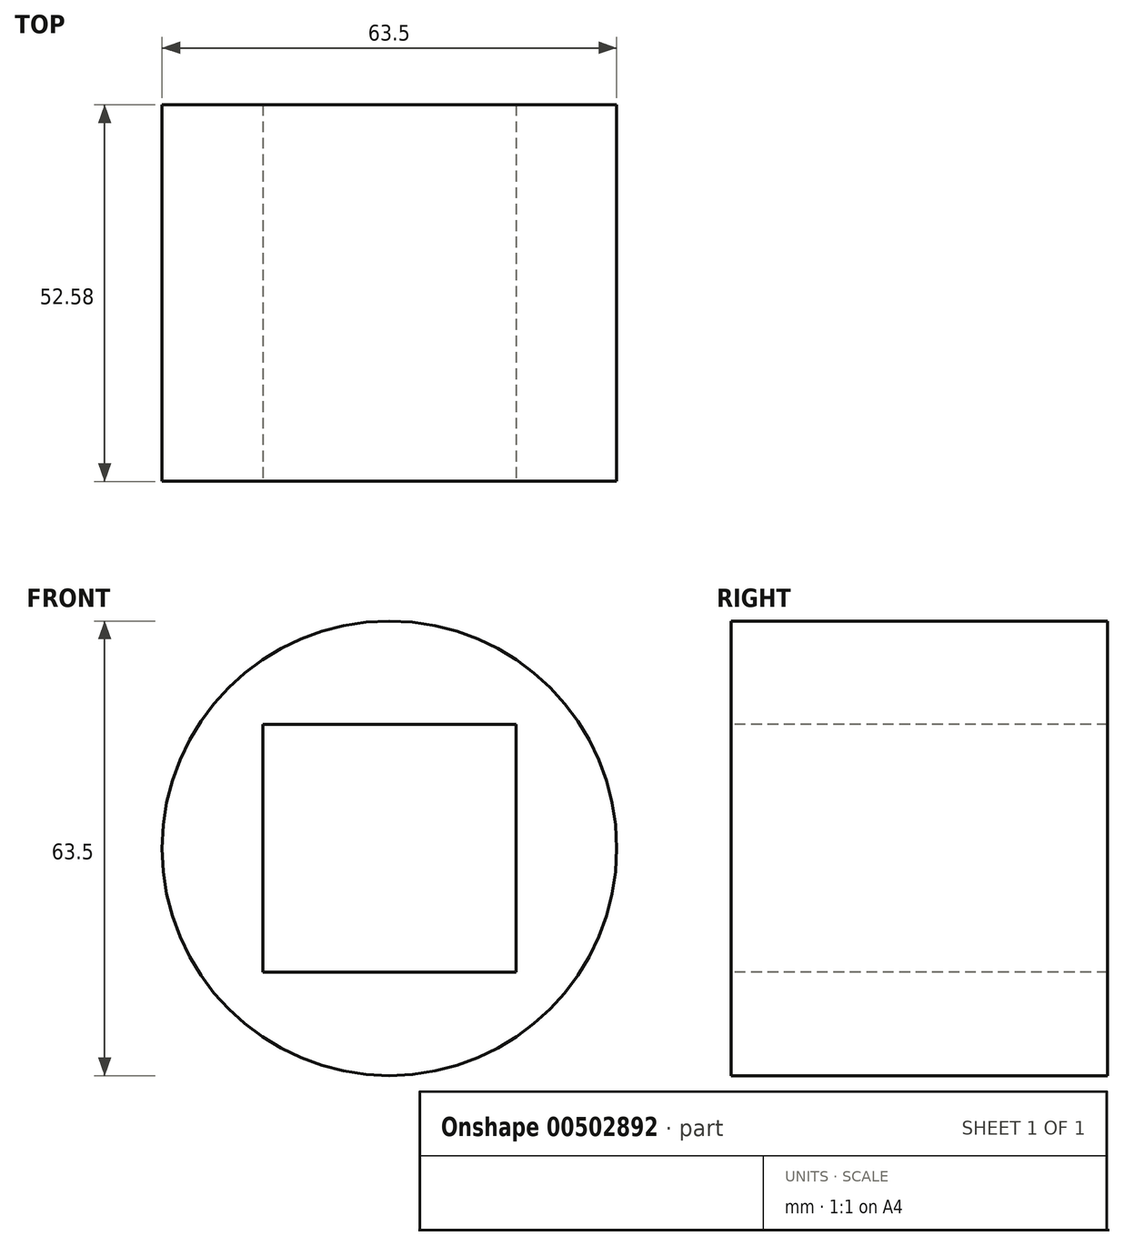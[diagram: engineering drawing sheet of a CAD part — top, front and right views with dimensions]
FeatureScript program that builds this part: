
annotation { "Feature Type Name" : "Feature", "Feature Type Description" : "" }
export const myFeature = defineFeature(function(context is Context, id is Id, definition is map)
    precondition{}
    {
        {
            var Q0;
            Q0=qCreatedBy(makeId("Front.planeOp"),FACE);
            var sketch = newSketch(context, id + "F0", { "sketchPlane" : qUnion([Q0])});
            skCircle(sketch, "E0", {"center": v(0, 0) * mm, "radius": 31.75 * mm});
            skSolve(sketch);
        }
        {
            var Q0;
            Q0=makeQuery(id+"F0.imprint","IMPRINT",FACE,{"disambiguationData":[TD([[makeQuery(id+"F0.imprint","IMPRINT",EDGE,{"derivedFrom":sQuery(id+"F0.wireOp",EDGE,"E0")}),1.0]])]});
            extrude(context, id + "F1", {"entities" : qUnion([Q0]), "depth" : 52.58 * mm});
        }
        {
            var Q0;
            Q0=makeQuery(id+"F1.opExtrude","CAP_FACE",FACE,{"disambiguationData":[OSD([sQuery(id+"F0.wireOp",EDGE,"E0")])],"isStart":false});
            var sketch = newSketch(context, id + "F2", { "sketchPlane" : qUnion([Q0])});
            skLineSegment(sketch, "E1.bottom", {"start": v(17.7, 17.29) * mm, "end": v(-17.7, 17.29) * mm});
            skLineSegment(sketch, "E1.top", {"start": v(17.7, -17.29) * mm, "end": v(-17.7, -17.29) * mm});
            skLineSegment(sketch, "E1.left", {"start": v(17.7, 17.29) * mm, "end": v(17.7, -17.29) * mm});
            skLineSegment(sketch, "E1.right", {"start": v(-17.7, 17.29) * mm, "end": v(-17.7, -17.29) * mm});
            skPoint(sketch, "E1.middle", {"position": v(0, 0) * mm});
            skSolve(sketch);
        }
        {
            var Q0;
            Q0=makeQuery(id+"F2.imprint","IMPRINT",FACE,{"disambiguationData":[TD([[makeQuery(id+"F2.imprint","IMPRINT",EDGE,{"derivedFrom":sQuery(id+"F2.wireOp",EDGE,"E1.bottom")}),1.0]])]});
            var Q1;
            Q1 = qSketchRegion(id + "F0", true);
            extrude(context, id + "F3", {"entities" : qUnion([Q0, Q1]), "operationType" : NewBodyOperationType.REMOVE, "oppositeDirection" : true, "depth" : 141.48 * mm});
        }
    });
